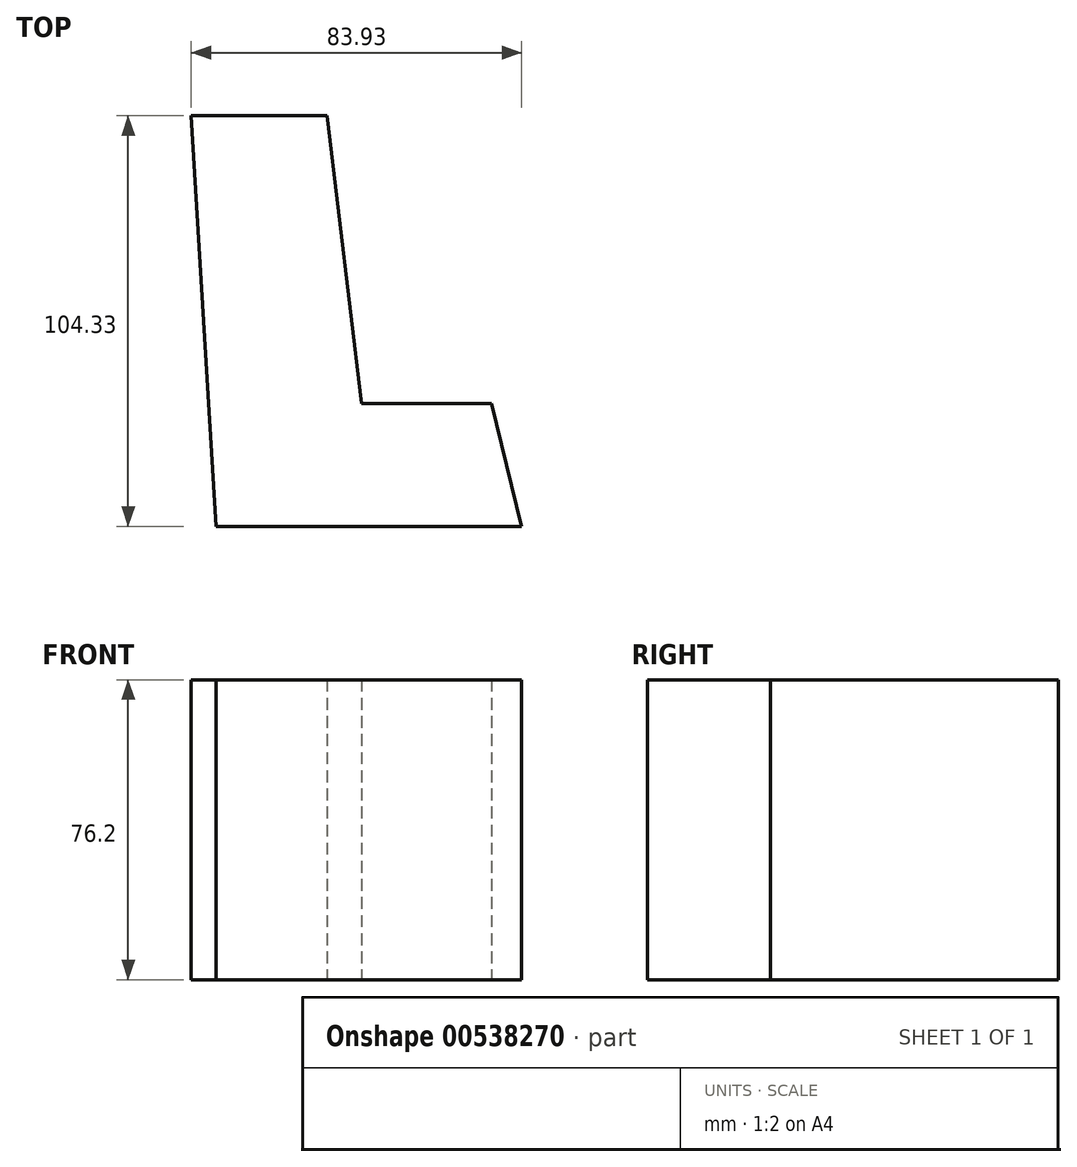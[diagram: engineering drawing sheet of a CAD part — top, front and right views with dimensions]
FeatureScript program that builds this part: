
annotation { "Feature Type Name" : "Feature", "Feature Type Description" : "" }
export const myFeature = defineFeature(function(context is Context, id is Id, definition is map)
    precondition{}
    {
        {
            var Q0;
            Q0=qCreatedBy(makeId("Top.planeOp"),FACE);
            var sketch = newSketch(context, id + "F0", { "sketchPlane" : qUnion([Q0])});
            skLineSegment(sketch, "E0", {"start": v(-55.24, 56.97) * mm, "end": v(-20.73, 56.97) * mm});
            skLineSegment(sketch, "E1", {"start": v(-55.24, 56.97) * mm, "end": v(-48.98, -47.36) * mm});
            skLineSegment(sketch, "E2", {"start": v(-20.73, 56.97) * mm, "end": v(-11.93, -16.16) * mm});
            skLineSegment(sketch, "E3", {"start": v(-11.93, -16.16) * mm, "end": v(21, -16.16) * mm});
            skLineSegment(sketch, "E4", {"start": v(-48.98, -47.36) * mm, "end": v(28.7, -47.36) * mm});
            skLineSegment(sketch, "E5", {"start": v(28.7, -47.36) * mm, "end": v(21, -16.16) * mm});
            skSolve(sketch);
        }
        {
            var Q0;
            Q0 = qSketchRegion(id + "F0", true);
            extrude(context, id + "F1", {"entities" : qUnion([Q0]), "depth" : 76.2 * mm, "offsetDistance" : 25.4 * mm});
        }
    });
